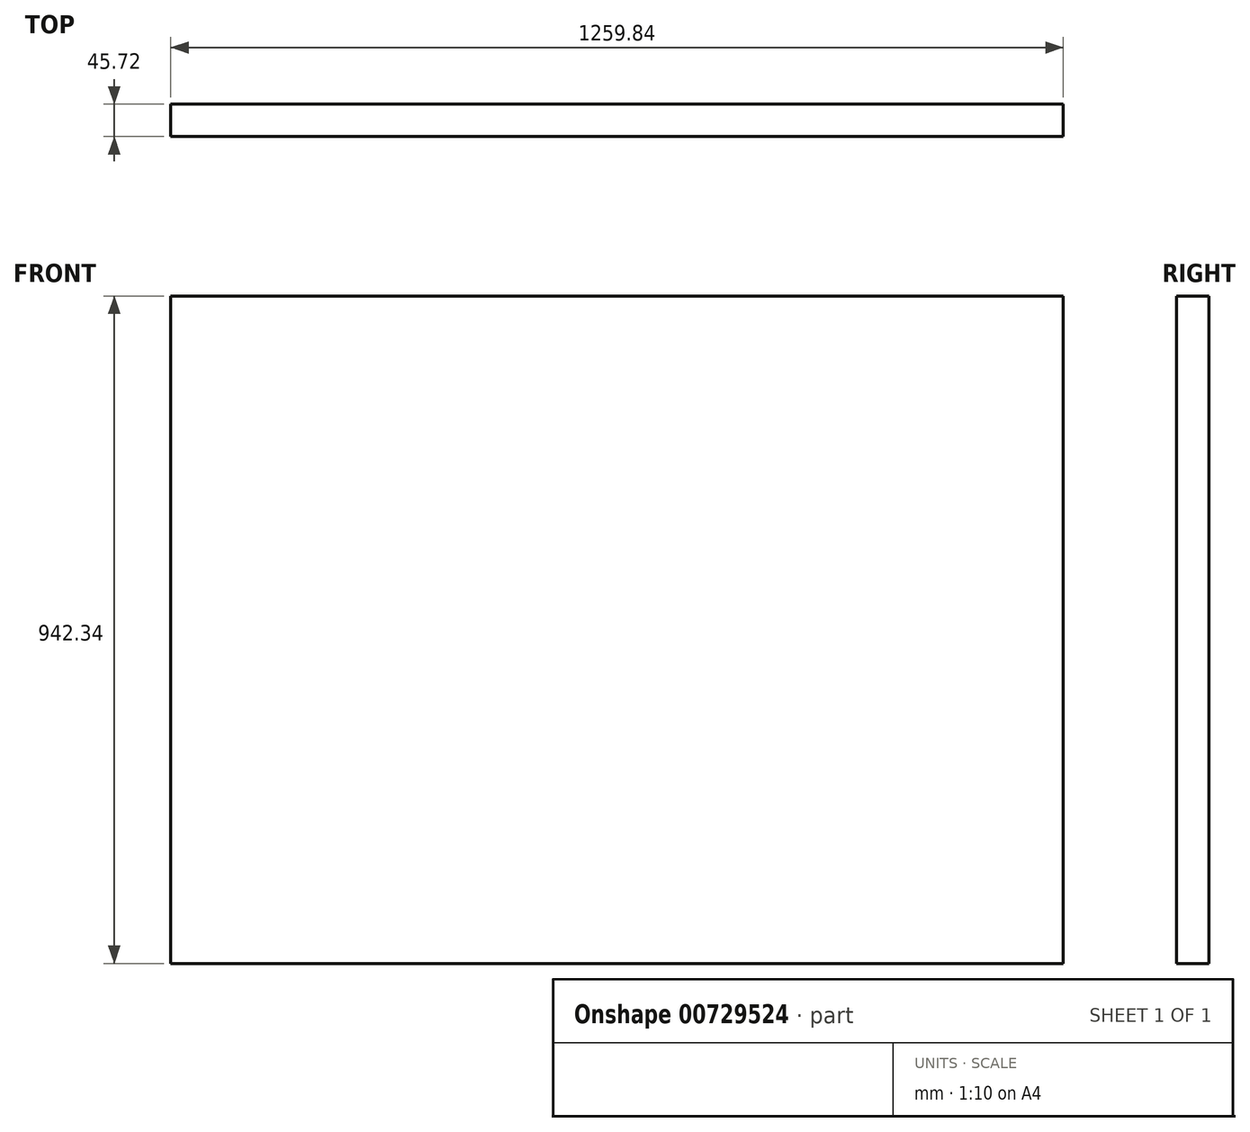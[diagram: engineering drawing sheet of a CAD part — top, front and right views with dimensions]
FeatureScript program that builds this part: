
annotation { "Feature Type Name" : "Feature", "Feature Type Description" : "" }
export const myFeature = defineFeature(function(context is Context, id is Id, definition is map)
    precondition{}
    {
        {
            var Q0;
            Q0=qCreatedBy(makeId("Front.planeOp"),FACE);
            var sketch = newSketch(context, id + "F0", { "sketchPlane" : qUnion([Q0])});
            skLineSegment(sketch, "E0.bottom", {"start": v(-52.38, 866.27) * mm, "end": v(1207.46, 866.27) * mm});
            skLineSegment(sketch, "E0.top", {"start": v(-52.38, -76.07) * mm, "end": v(1207.46, -76.07) * mm});
            skLineSegment(sketch, "E0.left", {"start": v(-52.38, 866.27) * mm, "end": v(-52.38, -76.07) * mm});
            skLineSegment(sketch, "E0.right", {"start": v(1207.46, 866.27) * mm, "end": v(1207.46, -76.07) * mm});
            skSolve(sketch);
        }
        {
            var Q0;
            Q0 = qSketchRegion(id + "F0", true);
            extrude(context, id + "F1", {"entities" : qUnion([Q0]), "depth" : 45.72 * mm, "offsetDistance" : 25.4 * mm});
        }
    });
